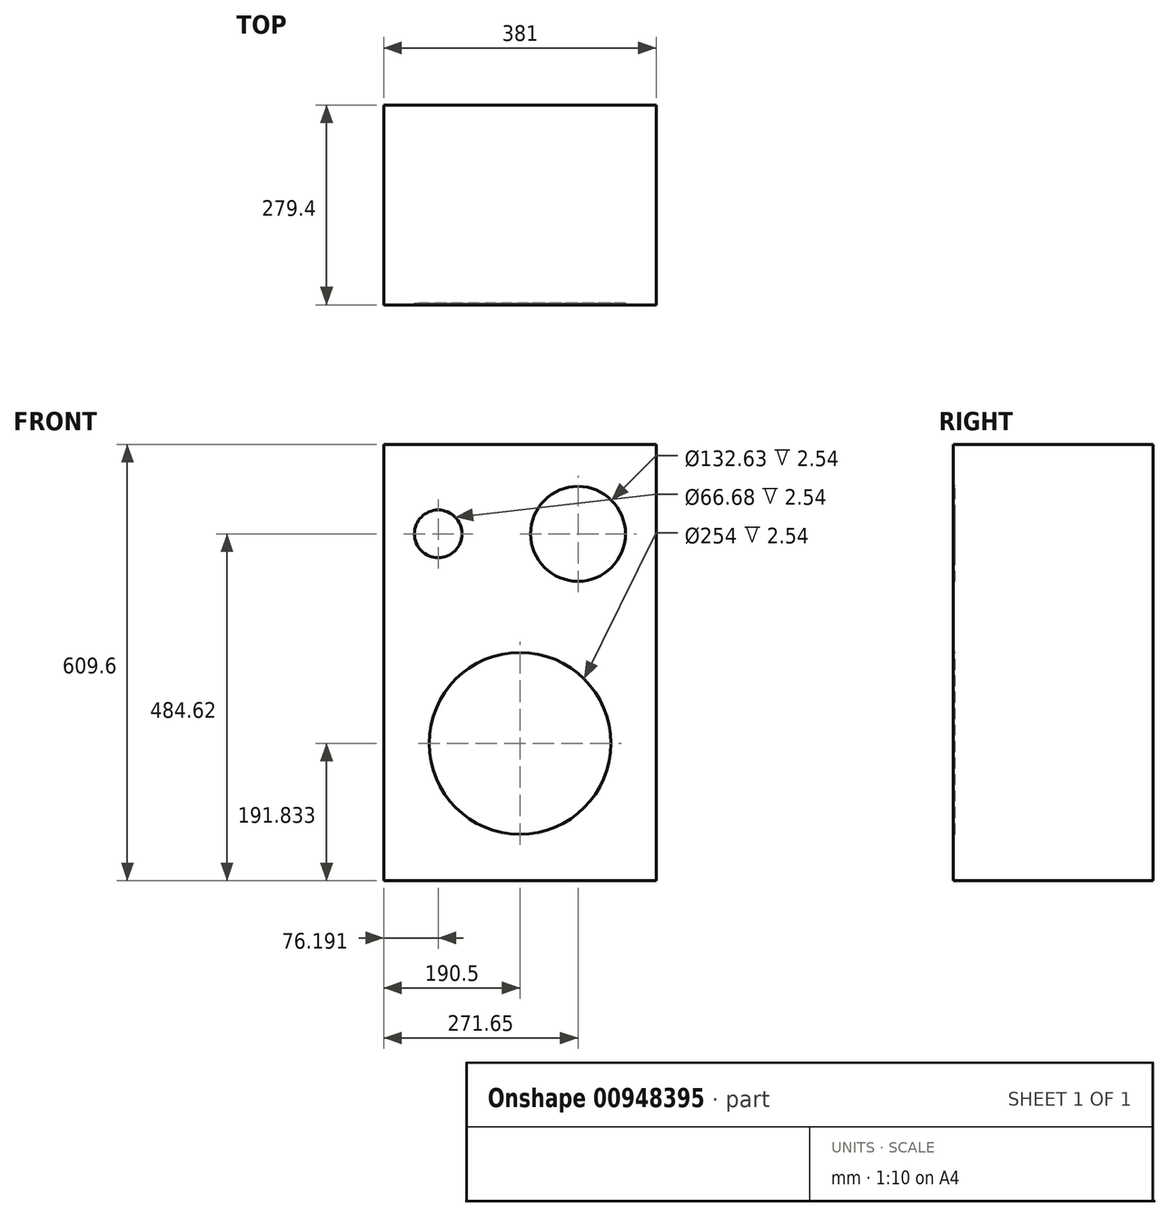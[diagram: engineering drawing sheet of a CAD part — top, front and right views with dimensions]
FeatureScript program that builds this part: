
annotation { "Feature Type Name" : "Feature", "Feature Type Description" : "" }
export const myFeature = defineFeature(function(context is Context, id is Id, definition is map)
    precondition{}
    {
        {
            var Q0;
            Q0=qCreatedBy(makeId("Top.planeOp"),FACE);
            var sketch = newSketch(context, id + "F0", { "sketchPlane" : qUnion([Q0])});
            skLineSegment(sketch, "E0.bottom", {"start": v(-190.5, 139.7) * mm, "end": v(190.5, 139.7) * mm});
            skLineSegment(sketch, "E0.top", {"start": v(-190.5, -139.7) * mm, "end": v(190.5, -139.7) * mm});
            skLineSegment(sketch, "E0.left", {"start": v(-190.5, 139.7) * mm, "end": v(-190.5, -139.7) * mm});
            skLineSegment(sketch, "E0.right", {"start": v(190.5, 139.7) * mm, "end": v(190.5, -139.7) * mm});
            skSolve(sketch);
        }
        {
            var Q0;
            Q0 = qSketchRegion(id + "F0", true);
            extrude(context, id + "F1", {"entities" : qUnion([Q0]), "depth" : 609.6 * mm, "offsetDistance" : 25.4 * mm});
        }
        {
            var Q0;
            Q0=makeQuery(id+"F1.opExtrude","SWEPT_FACE",FACE,{"disambiguationData":[OSD([sQuery(id+"F0.wireOp",EDGE,"E0.top")])]});
            var sketch = newSketch(context, id + "F2", { "sketchPlane" : qUnion([Q0])});
            skCircle(sketch, "E1", {"center": v(0, 191.83) * mm, "radius": 127 * mm});
            skCircle(sketch, "E2", {"center": v(-114.3, 484.62) * mm, "radius": 33.34 * mm});
            skCircle(sketch, "E3", {"center": v(81.15, 484.62) * mm, "radius": 66.32 * mm});
            skSolve(sketch);
        }
        {
            var Q0;
            Q0 = qSketchRegion(id + "F2", true);
            extrude(context, id + "F3", {"entities" : qUnion([Q0]), "operationType" : NewBodyOperationType.REMOVE, "oppositeDirection" : true, "depth" : 2.54 * mm, "offsetDistance" : 25.4 * mm});
        }
    });
